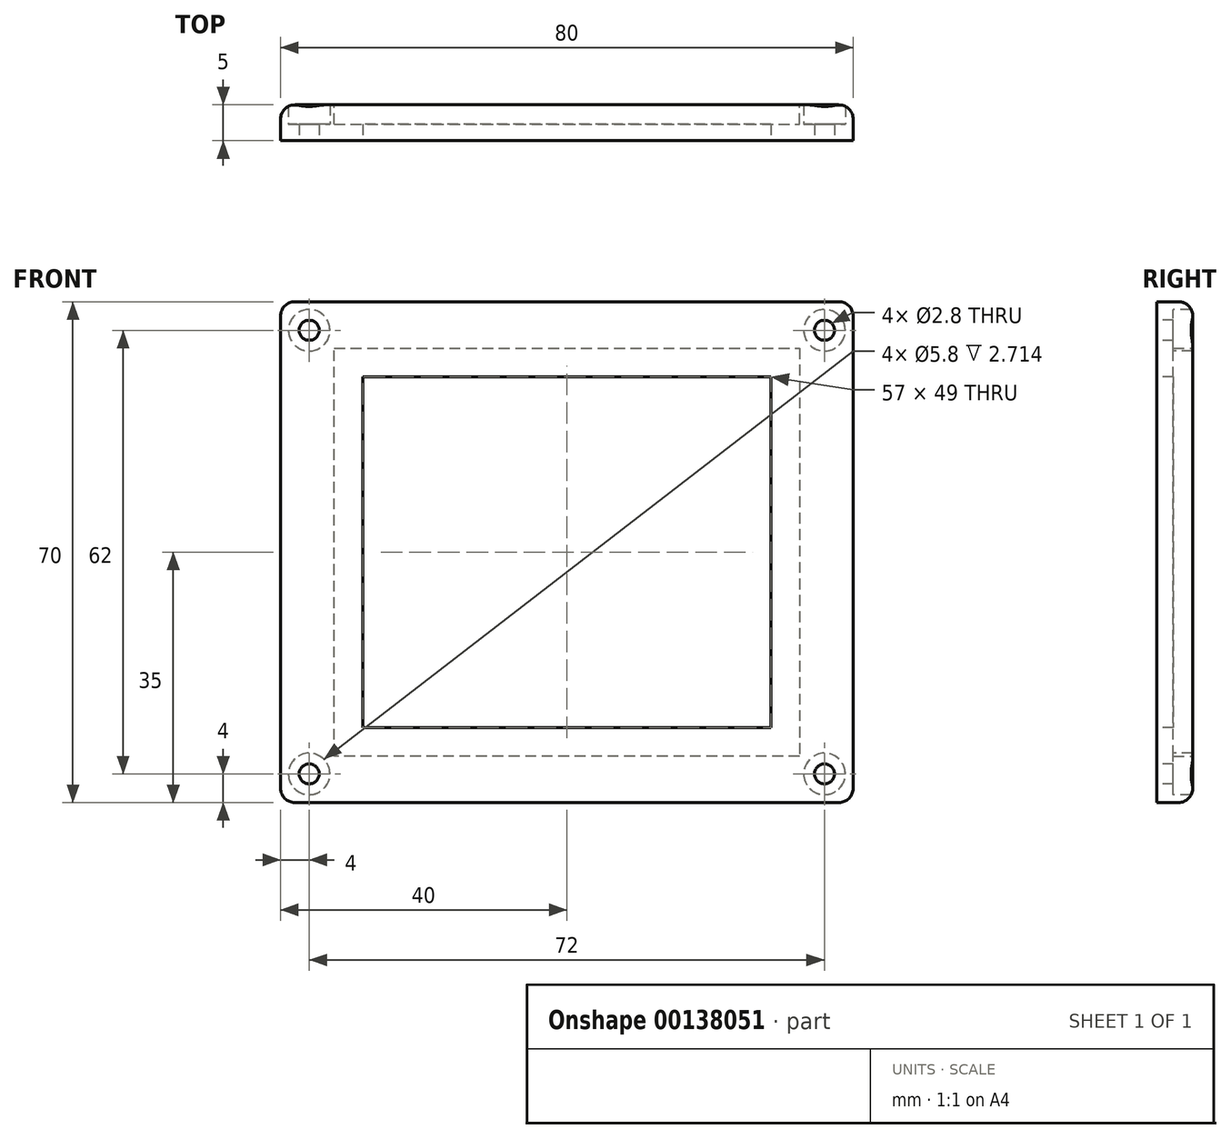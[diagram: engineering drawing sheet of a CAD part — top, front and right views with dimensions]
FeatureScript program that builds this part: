
annotation { "Feature Type Name" : "Feature", "Feature Type Description" : "" }
export const myFeature = defineFeature(function(context is Context, id is Id, definition is map)
    precondition{}
    {
        {
            var Q0;
            Q0=qCreatedBy(makeId("Front.planeOp"),FACE);
            var sketch = newSketch(context, id + "F0", { "sketchPlane" : qUnion([Q0])});
            skLineSegment(sketch, "E0.bottom", {"start": v(40, -35) * mm, "end": v(-40, -35) * mm});
            skLineSegment(sketch, "E0.top", {"start": v(40, 35) * mm, "end": v(-40, 35) * mm});
            skLineSegment(sketch, "E0.left", {"start": v(40, -35) * mm, "end": v(40, 35) * mm});
            skLineSegment(sketch, "E0.right", {"start": v(-40, -35) * mm, "end": v(-40, 35) * mm});
            skPoint(sketch, "E0.middle", {"position": v(0, 0) * mm});
            skLineSegment(sketch, "E1", {"start": v(32.5, -28.5) * mm, "end": v(-32.5, -28.5) * mm});
            skLineSegment(sketch, "E2", {"start": v(-32.5, -28.5) * mm, "end": v(-32.5, 28.5) * mm});
            skLineSegment(sketch, "E3", {"start": v(-32.5, 28.5) * mm, "end": v(32.5, 28.5) * mm});
            skLineSegment(sketch, "E4", {"start": v(32.5, 28.5) * mm, "end": v(32.5, -28.5) * mm});
            skLineSegment(sketch, "E5", {"start": v(-30.5, 26.5) * mm, "end": v(-30.5, -26.5) * mm});
            skLineSegment(sketch, "E6", {"start": v(-30.5, -26.5) * mm, "end": v(30.5, -26.5) * mm});
            skLineSegment(sketch, "E7", {"start": v(30.5, -26.5) * mm, "end": v(30.5, 26.5) * mm});
            skLineSegment(sketch, "E8", {"start": v(30.5, 26.5) * mm, "end": v(-30.5, 26.5) * mm});
            skSolve(sketch);
        }
        {
            var Q0;
            Q0=makeQuery(id+"F0.imprint","IMPRINT",FACE,{"disambiguationData":[TD([[makeQuery(id+"F0.imprint","IMPRINT",EDGE,{"derivedFrom":sQuery(id+"F0.wireOp",EDGE,"E0.bottom")}),-1.0]])]});
            extrude(context, id + "F1", {"entities" : qUnion([Q0]), "depth" : 5 * mm});
        }
        {
            var Q0;
            Q0=makeQuery(id+"F1.opExtrude","CAP_EDGE",EDGE,{"disambiguationData":[OSD([sQuery(id+"F0.wireOp",EDGE,"E0.top")])],"isStart":true});
            var Q1;
            Q1=makeQuery(id+"F1.opExtrude","CAP_EDGE",EDGE,{"disambiguationData":[OSD([sQuery(id+"F0.wireOp",EDGE,"E0.right")])],"isStart":true});
            var Q2;
            Q2=makeQuery(id+"F1.opExtrude","SWEPT_EDGE",EDGE,{"disambiguationData":[OSD([sQuery(id+"F0.wireOp",EDGE,"E0.top"),sQuery(id+"F0.wireOp",EDGE,"E0.right")])]});
            var Q3;
            Q3=makeQuery(id+"F1.opExtrude","CAP_EDGE",EDGE,{"disambiguationData":[OSD([sQuery(id+"F0.wireOp",EDGE,"E0.bottom")])],"isStart":true});
            var Q4;
            Q4=makeQuery(id+"F1.opExtrude","SWEPT_EDGE",EDGE,{"disambiguationData":[OSD([sQuery(id+"F0.wireOp",EDGE,"E0.bottom"),sQuery(id+"F0.wireOp",EDGE,"E0.right")])]});
            var Q5;
            Q5=makeQuery(id+"F1.opExtrude","CAP_EDGE",EDGE,{"disambiguationData":[OSD([sQuery(id+"F0.wireOp",EDGE,"E0.left")])],"isStart":true});
            var Q6;
            Q6=makeQuery(id+"F1.opExtrude","SWEPT_EDGE",EDGE,{"disambiguationData":[OSD([sQuery(id+"F0.wireOp",EDGE,"E0.bottom"),sQuery(id+"F0.wireOp",EDGE,"E0.left")])]});
            var Q7;
            Q7=makeQuery(id+"F1.opExtrude","SWEPT_EDGE",EDGE,{"disambiguationData":[OSD([sQuery(id+"F0.wireOp",EDGE,"E0.top"),sQuery(id+"F0.wireOp",EDGE,"E0.left")])]});
            fillet(context, id + "F2", {"entities" : qUnion([Q0, Q1, Q2, Q3, Q4, Q5, Q6, Q7]), "radius" : 2 * mm, "tangentPropagation" : true, "allowEdgeOverflow" : false});
        }
        {
            var Q0;
            Q0=makeQuery(id+"F1.opExtrude","CAP_FACE",FACE,{"disambiguationData":[OSD([sQuery(id+"F0.wireOp",EDGE,"E0.bottom"),sQuery(id+"F0.wireOp",EDGE,"E0.top"),sQuery(id+"F0.wireOp",EDGE,"E0.left"),sQuery(id+"F0.wireOp",EDGE,"E0.right")])],"isStart":true});
            cPlane(context, id + "F3", {"entities" : qUnion([Q0]), "cplaneType" : CPlaneType.OFFSET, "offset" : 0 * mm, "width" : 150 * mm, "height" : 150 * mm});
        }
        {
            var Q0;
            Q0=qCreatedBy(id+"F3.planeOp",FACE);
            var sketch = newSketch(context, id + "F4", { "sketchPlane" : qUnion([Q0])});
            skPoint(sketch, "E9", {"position": v(-36, -31) * mm});
            skPoint(sketch, "E10", {"position": v(-36, 31) * mm});
            skPoint(sketch, "E11", {"position": v(36, 31) * mm});
            skPoint(sketch, "E12", {"position": v(36, -31) * mm});
            skSolve(sketch);
        }
        {
            var Q0;
            Q0=sQuery(id+"F4.wireOp",VERTEX,"E9");
            var Q1;
            Q1=sQuery(id+"F4.wireOp",VERTEX,"E10");
            var Q2;
            Q2=sQuery(id+"F4.wireOp",VERTEX,"E11");
            var Q3;
            Q3=sQuery(id+"F4.wireOp",VERTEX,"E12");
            var Q4;
            Q4=makeQuery(id+"F1.opExtrude","SWEPT_BODY",BODY,{"disambiguationData":[OSD([sQuery(id+"F0.wireOp",EDGE,"E0.bottom"),sQuery(id+"F0.wireOp",EDGE,"E0.top"),sQuery(id+"F0.wireOp",EDGE,"E0.left"),sQuery(id+"F0.wireOp",EDGE,"E0.right")])]});
            hole(context, id + "F5", {"style" : HoleStyle.C_BORE, "endStyle" : HoleEndStyle.BLIND, "holeDiameter" : 2.8 * mm, "cBoreDiameter" : 5.8 * mm, "cBoreDepth" : 2.5 * mm, "holeDepth" : 5 * mm, "locations" : qUnion([Q0, Q1, Q2, Q3]), "scope" : qUnion([Q4]), "tappedDepth" : 12 * mm, "tapClearance" : 3, "startStyle" : HoleStartStyle.PART});
        }
        {
            var Q0;
            Q0=makeQuery(id+"F1.opExtrude","CAP_FACE",FACE,{"disambiguationData":[OSD([sQuery(id+"F0.wireOp",EDGE,"E0.bottom"),sQuery(id+"F0.wireOp",EDGE,"E0.top"),sQuery(id+"F0.wireOp",EDGE,"E0.left"),sQuery(id+"F0.wireOp",EDGE,"E0.right"),sQuery(id+"F0.wireOp",EDGE,"E1"),sQuery(id+"F0.wireOp",EDGE,"E2"),sQuery(id+"F0.wireOp",EDGE,"E3"),sQuery(id+"F0.wireOp",EDGE,"E4")])],"isStart":false});
            cPlane(context, id + "F6", {"entities" : qUnion([Q0]), "cplaneType" : CPlaneType.OFFSET, "offset" : 0 * mm, "width" : 150 * mm, "height" : 150 * mm});
        }
        {
            var Q0;
            Q0=qCreatedBy(id+"F6.planeOp",FACE);
            var sketch = newSketch(context, id + "F7", { "sketchPlane" : qUnion([Q0])});
            skLineSegment(sketch, "E13.bottom", {"start": v(40, -35) * mm, "end": v(-40, -35) * mm});
            skLineSegment(sketch, "E13.top", {"start": v(40, 35) * mm, "end": v(-40, 35) * mm});
            skLineSegment(sketch, "E13.left", {"start": v(40, -35) * mm, "end": v(40, 35) * mm});
            skLineSegment(sketch, "E13.right", {"start": v(-40, -35) * mm, "end": v(-40, 35) * mm});
            skPoint(sketch, "E13.middle", {"position": v(0, 0) * mm});
            skLineSegment(sketch, "E14", {"start": v(-28.5, 24.5) * mm, "end": v(-28.5, -24.5) * mm});
            skLineSegment(sketch, "E15", {"start": v(-28.5, -24.5) * mm, "end": v(28.5, -24.5) * mm});
            skLineSegment(sketch, "E16", {"start": v(28.5, -24.5) * mm, "end": v(28.5, 24.5) * mm});
            skLineSegment(sketch, "E17", {"start": v(28.5, 24.5) * mm, "end": v(-28.5, 24.5) * mm});
            skLineSegment(sketch, "E18.bottom", {"start": v(-32.5, -28.5) * mm, "end": v(32.5, -28.5) * mm});
            skLineSegment(sketch, "E18.top", {"start": v(-32.5, 28.5) * mm, "end": v(32.5, 28.5) * mm});
            skLineSegment(sketch, "E18.left", {"start": v(-32.5, -28.5) * mm, "end": v(-32.5, 28.5) * mm});
            skLineSegment(sketch, "E18.right", {"start": v(32.5, -28.5) * mm, "end": v(32.5, 28.5) * mm});
            skSolve(sketch);
        }
        {
            var Q0;
            Q0=makeQuery(id+"F7.imprint","IMPRINT",FACE,{"disambiguationData":[TD([[makeQuery(id+"F7.imprint","IMPRINT",EDGE,{"derivedFrom":sQuery(id+"F7.wireOp",EDGE,"E14")}),-1.0]])]});
            extrude(context, id + "F8", {"entities" : qUnion([Q0]), "operationType" : NewBodyOperationType.ADD, "oppositeDirection" : true, "depth" : 2.3 * mm});
        }
    });
